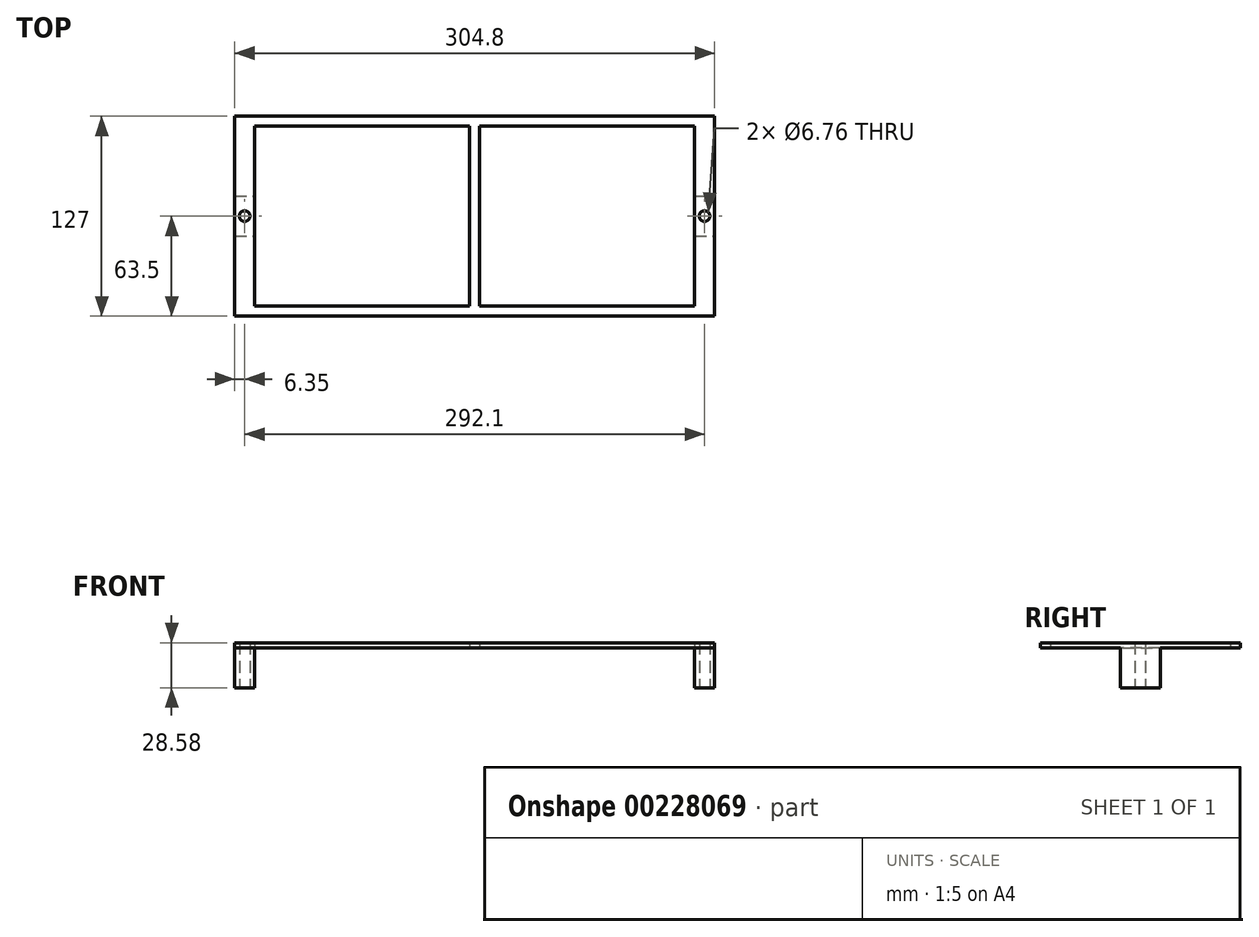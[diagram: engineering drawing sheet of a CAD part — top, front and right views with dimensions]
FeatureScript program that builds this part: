
annotation { "Feature Type Name" : "Feature", "Feature Type Description" : "" }
export const myFeature = defineFeature(function(context is Context, id is Id, definition is map)
    precondition{}
    {
        {
            var Q0;
            Q0=qCreatedBy(makeId("Top.planeOp"),FACE);
            var sketch = newSketch(context, id + "F0", { "sketchPlane" : qUnion([Q0])});
            skLineSegment(sketch, "E0.bottom", {"start": v(0, 0) * mm, "end": v(304.8, 0) * mm});
            skLineSegment(sketch, "E0.top", {"start": v(0, 127) * mm, "end": v(304.8, 127) * mm});
            skLineSegment(sketch, "E0.left", {"start": v(0, 0) * mm, "end": v(0, 127) * mm});
            skLineSegment(sketch, "E0.right", {"start": v(304.8, 0) * mm, "end": v(304.8, 127) * mm});
            skLineSegment(sketch, "E1.bottom", {"start": v(12.7, 6.35) * mm, "end": v(149.22, 6.35) * mm});
            skLineSegment(sketch, "E1.top", {"start": v(12.7, 120.65) * mm, "end": v(149.22, 120.65) * mm});
            skLineSegment(sketch, "E1.left", {"start": v(12.7, 6.35) * mm, "end": v(12.7, 120.65) * mm});
            skLineSegment(sketch, "E1.right", {"start": v(149.22, 6.35) * mm, "end": v(149.22, 120.65) * mm});
            skLineSegment(sketch, "E2.bottom", {"start": v(155.57, 120.65) * mm, "end": v(292.1, 120.65) * mm});
            skLineSegment(sketch, "E2.top", {"start": v(155.57, 6.35) * mm, "end": v(292.1, 6.35) * mm});
            skLineSegment(sketch, "E2.left", {"start": v(155.57, 120.65) * mm, "end": v(155.57, 6.35) * mm});
            skLineSegment(sketch, "E2.right", {"start": v(292.1, 120.65) * mm, "end": v(292.1, 6.35) * mm});
            skSolve(sketch);
        }
        {
            var Q0;
            Q0 = qSketchRegion(id + "F0", true);
            extrude(context, id + "F1", {"entities" : qUnion([Q0]), "depth" : 3.17 * mm});
        }
        {
            var Q0;
            Q0=makeQuery(id+"F1.opExtrude","CAP_FACE",FACE,{"disambiguationData":[OSD([sQuery(id+"F0.wireOp",EDGE,"E0.bottom"),sQuery(id+"F0.wireOp",EDGE,"E0.top"),sQuery(id+"F0.wireOp",EDGE,"E0.left"),sQuery(id+"F0.wireOp",EDGE,"E0.right"),sQuery(id+"F0.wireOp",EDGE,"E1.bottom"),sQuery(id+"F0.wireOp",EDGE,"E1.top"),sQuery(id+"F0.wireOp",EDGE,"E1.left"),sQuery(id+"F0.wireOp",EDGE,"E1.right"),sQuery(id+"F0.wireOp",EDGE,"E2.bottom"),sQuery(id+"F0.wireOp",EDGE,"E2.top"),sQuery(id+"F0.wireOp",EDGE,"E2.left"),sQuery(id+"F0.wireOp",EDGE,"E2.right")])],"isStart":true});
            var sketch = newSketch(context, id + "F2", { "sketchPlane" : qUnion([Q0])});
            skLineSegment(sketch, "E3.bottom", {"start": v(0, -50.8) * mm, "end": v(12.7, -50.8) * mm});
            skLineSegment(sketch, "E3.top", {"start": v(0, -76.2) * mm, "end": v(12.7, -76.2) * mm});
            skLineSegment(sketch, "E3.left", {"start": v(0, -50.8) * mm, "end": v(0, -76.2) * mm});
            skLineSegment(sketch, "E3.right", {"start": v(12.7, -50.8) * mm, "end": v(12.7, -76.2) * mm});
            skLineSegment(sketch, "E4.bottom", {"start": v(292.1, -50.8) * mm, "end": v(304.8, -50.8) * mm});
            skLineSegment(sketch, "E4.top", {"start": v(292.1, -76.2) * mm, "end": v(304.8, -76.2) * mm});
            skLineSegment(sketch, "E4.left", {"start": v(292.1, -50.8) * mm, "end": v(292.1, -76.2) * mm});
            skLineSegment(sketch, "E4.right", {"start": v(304.8, -50.8) * mm, "end": v(304.8, -76.2) * mm});
            skSolve(sketch);
        }
        {
            var Q0;
            Q0 = qSketchRegion(id + "F2", true);
            extrude(context, id + "F3", {"entities" : qUnion([Q0]), "operationType" : NewBodyOperationType.ADD, "depth" : 25.4 * mm});
        }
        {
            var Q0;
            Q0=makeQuery(id+"F3.opExtrude","CAP_FACE",FACE,{"disambiguationData":[OSD([sQuery(id+"F2.wireOp",EDGE,"E3.bottom"),sQuery(id+"F2.wireOp",EDGE,"E3.top"),sQuery(id+"F2.wireOp",EDGE,"E3.left"),sQuery(id+"F2.wireOp",EDGE,"E3.right")])],"isStart":false});
            var sketch = newSketch(context, id + "F4", { "sketchPlane" : qUnion([Q0])});
            skPoint(sketch, "E5", {"position": v(6.35, -63.5) * mm});
            skPoint(sketch, "E6", {"position": v(298.45, -63.5) * mm});
            skLineSegment(sketch, "E7", {"start": v(6.35, -50.8) * mm, "end": v(6.35, -76.2) * mm, "construction": true});
            skLineSegment(sketch, "E8", {"start": v(298.45, -50.8) * mm, "end": v(298.45, -76.2) * mm, "construction": true});
            skSolve(sketch);
        }
        {
            var Q0;
            Q0=sQuery(id+"F4.wireOp",VERTEX,"E5");
            var Q1;
            Q1=sQuery(id+"F4.wireOp",VERTEX,"E6");
            var Q2;
            Q2=makeQuery(id+"F1.opExtrude","SWEPT_BODY",BODY,{"disambiguationData":[OSD([sQuery(id+"F0.wireOp",EDGE,"E0.bottom"),sQuery(id+"F0.wireOp",EDGE,"E0.top"),sQuery(id+"F0.wireOp",EDGE,"E0.left"),sQuery(id+"F0.wireOp",EDGE,"E0.right"),sQuery(id+"F0.wireOp",EDGE,"E1.bottom"),sQuery(id+"F0.wireOp",EDGE,"E1.top"),sQuery(id+"F0.wireOp",EDGE,"E1.left"),sQuery(id+"F0.wireOp",EDGE,"E1.right"),sQuery(id+"F0.wireOp",EDGE,"E2.bottom"),sQuery(id+"F0.wireOp",EDGE,"E2.top"),sQuery(id+"F0.wireOp",EDGE,"E2.left"),sQuery(id+"F0.wireOp",EDGE,"E2.right")])]});
            hole(context, id + "F5", {"style" : HoleStyle.SIMPLE, "endStyle" : HoleEndStyle.THROUGH, "standardTappedOrClearance" : lookupTablePath({ "standard" : "ANSI", "fit" : "Normal (ASME)", "size" : "1/4", "type" : "Clearance" }), "standardBlindInLast" : lookupTablePath({ "fit" : "Free", "standard" : "ANSI", "size" : "1/4", "type" : "Clearance" }), "holeDiameter" : 6.76 * mm, "locations" : qUnion([Q0, Q1]), "scope" : qUnion([Q2]), "isTappedThrough" : true});
        }
    });
